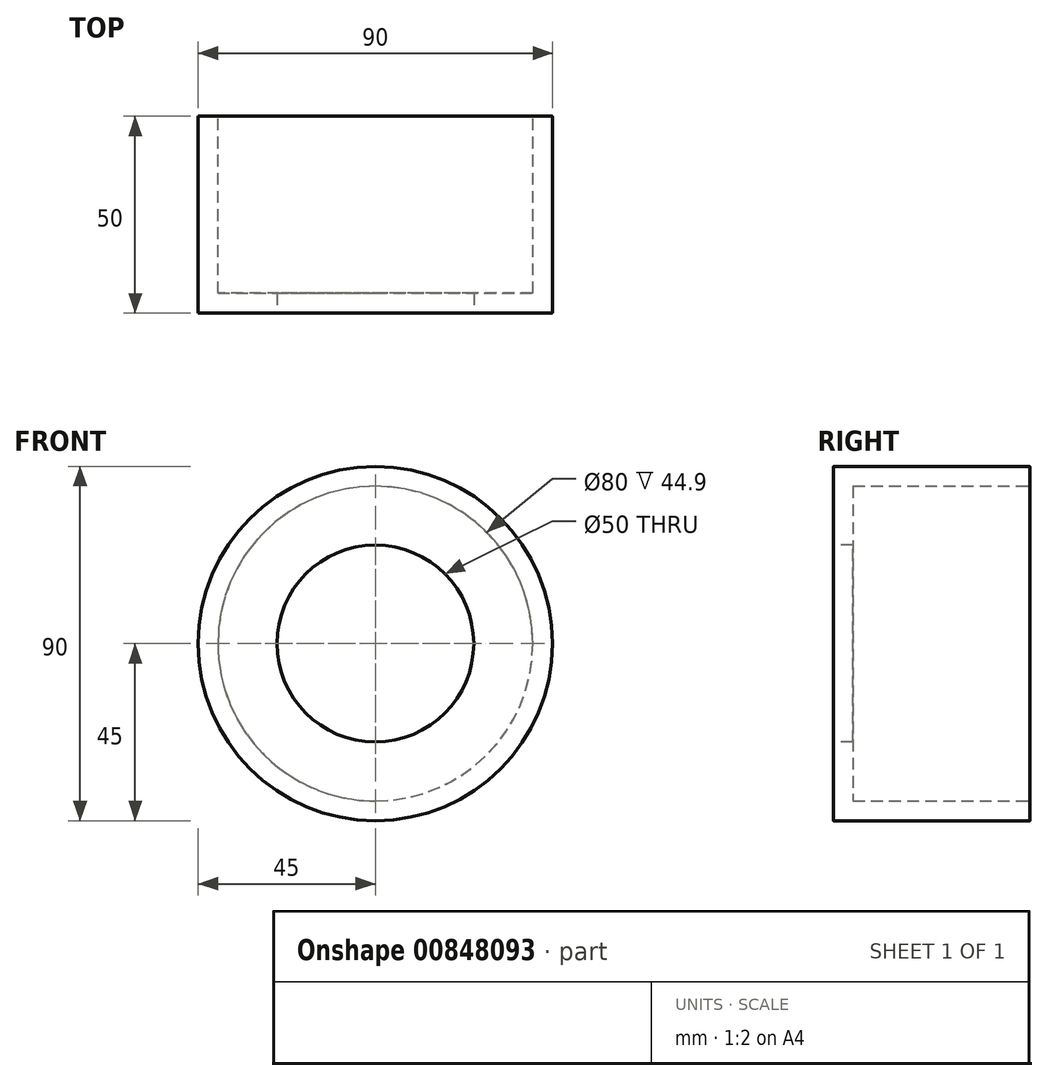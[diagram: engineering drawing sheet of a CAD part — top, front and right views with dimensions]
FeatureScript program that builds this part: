
annotation { "Feature Type Name" : "Feature", "Feature Type Description" : "" }
export const myFeature = defineFeature(function(context is Context, id is Id, definition is map)
    precondition{}
    {
        {
            var Q0;
            Q0=qCreatedBy(makeId("Top.planeOp"),FACE);
            var sketch = newSketch(context, id + "F0", { "sketchPlane" : qUnion([Q0])});
            skLineSegment(sketch, "E0", {"start": v(0, -23.24) * mm, "end": v(-45, -23.24) * mm});
            skLineSegment(sketch, "E1", {"start": v(-45, -23.24) * mm, "end": v(-45, 26.76) * mm});
            skLineSegment(sketch, "E2", {"start": v(-45, 26.76) * mm, "end": v(-40, 26.76) * mm});
            skLineSegment(sketch, "E3", {"start": v(-40, 26.76) * mm, "end": v(-40, -18.24) * mm});
            skLineSegment(sketch, "E4", {"start": v(-40, -18.24) * mm, "end": v(0, -18.24) * mm});
            skLineSegment(sketch, "E5", {"start": v(0, -18.24) * mm, "end": v(0, -23.24) * mm});
            skSolve(sketch);
        }
        {
            var Q0;
            Q0 = qSketchRegion(id + "F0", true);
            var Q1;
            Q1=sQuery(id+"F0.wireOp",EDGE,"E5");
            revolve(context, id + "F1", {"surfaceOperationType" : NewSurfaceOperationType.NEW, "entities" : qUnion([Q0]), "axis" : qUnion([Q1]), "revolveType" : RevolveType.FULL});
        }
        {
            var Q0;
            Q0=makeQuery(id+"F1.opRevolve","SWEPT_FACE",FACE,{"disambiguationData":[OSD([sQuery(id+"F0.wireOp",EDGE,"E0")])]});
            var sketch = newSketch(context, id + "F2", { "sketchPlane" : qUnion([Q0])});
            skPoint(sketch, "E6", {"position": v(0, 0) * mm});
            skSolve(sketch);
        }
        {
            var Q0;
            Q0=sQuery(id+"F2.wireOp",VERTEX,"E6");
            var Q1;
            Q1=makeQuery(id+"F1.opRevolve","SWEPT_BODY",BODY,{"disambiguationData":[OSD([sQuery(id+"F0.wireOp",EDGE,"E0"),sQuery(id+"F0.wireOp",EDGE,"E1"),sQuery(id+"F0.wireOp",EDGE,"E2"),sQuery(id+"F0.wireOp",EDGE,"E3"),sQuery(id+"F0.wireOp",EDGE,"E4"),sQuery(id+"F0.wireOp",EDGE,"E5")])]});
            hole(context, id + "F3", {"style" : HoleStyle.SIMPLE, "endStyle" : HoleEndStyle.THROUGH, "holeDiameter" : 50 * mm, "majorDiameter" : 5 * mm, "isTappedThrough" : true, "tappedDepth" : 12 * mm, "tapClearance" : 3, "locations" : qUnion([Q0]), "scope" : qUnion([Q1])});
        }
        {
            var Q0;
            Q0=makeQuery(id+"F3.hole-0.boolean.opBoolean","COPY",EDGE,{"derivedFrom":makeQuery(id+"F3.hole-0.opRevolve","SWEPT_EDGE",EDGE,{"disambiguationData":[OSD([sQuery(id+"F3.hole-0.sketch.wireOp",EDGE,"core_line_2"),sQuery(id+"F3.hole-0.sketch.wireOp",EDGE,"core_line_3")])]})});
            var Q1;
            Q1=makeQuery(id+"F1.opRevolve","SWEPT_EDGE",EDGE,{"disambiguationData":[OSD([sQuery(id+"F0.wireOp",EDGE,"E0"),sQuery(id+"F0.wireOp",EDGE,"E1")])]});
            var Q2;
            Q2=makeQuery(id+"F3.hole-0.boolean.opBoolean","INTERSECT",EDGE,{"derivedFrom":[makeQuery(id+"F1.opRevolve","SWEPT_FACE",FACE,{"disambiguationData":[OSD([sQuery(id+"F0.wireOp",EDGE,"E4")])]}),makeQuery(id+"F3.hole-0.opRevolve","SWEPT_FACE",FACE,{"disambiguationData":[OSD([sQuery(id+"F3.hole-0.sketch.wireOp",EDGE,"core_line_2")])]})]});
            var Q3;
            Q3=makeQuery(id+"F1.opRevolve","SWEPT_EDGE",EDGE,{"disambiguationData":[OSD([sQuery(id+"F0.wireOp",EDGE,"E2"),sQuery(id+"F0.wireOp",EDGE,"E3")])]});
            var Q4;
            Q4=makeQuery(id+"F1.opRevolve","SWEPT_EDGE",EDGE,{"disambiguationData":[OSD([sQuery(id+"F0.wireOp",EDGE,"E1"),sQuery(id+"F0.wireOp",EDGE,"E2")])]});
            fillet(context, id + "F4", {"entities" : qUnion([Q0, Q1, Q2, Q3, Q4]), "radius" : 0.1 * mm, "tangentPropagation" : true, "allowEdgeOverflow" : false});
        }
    });
